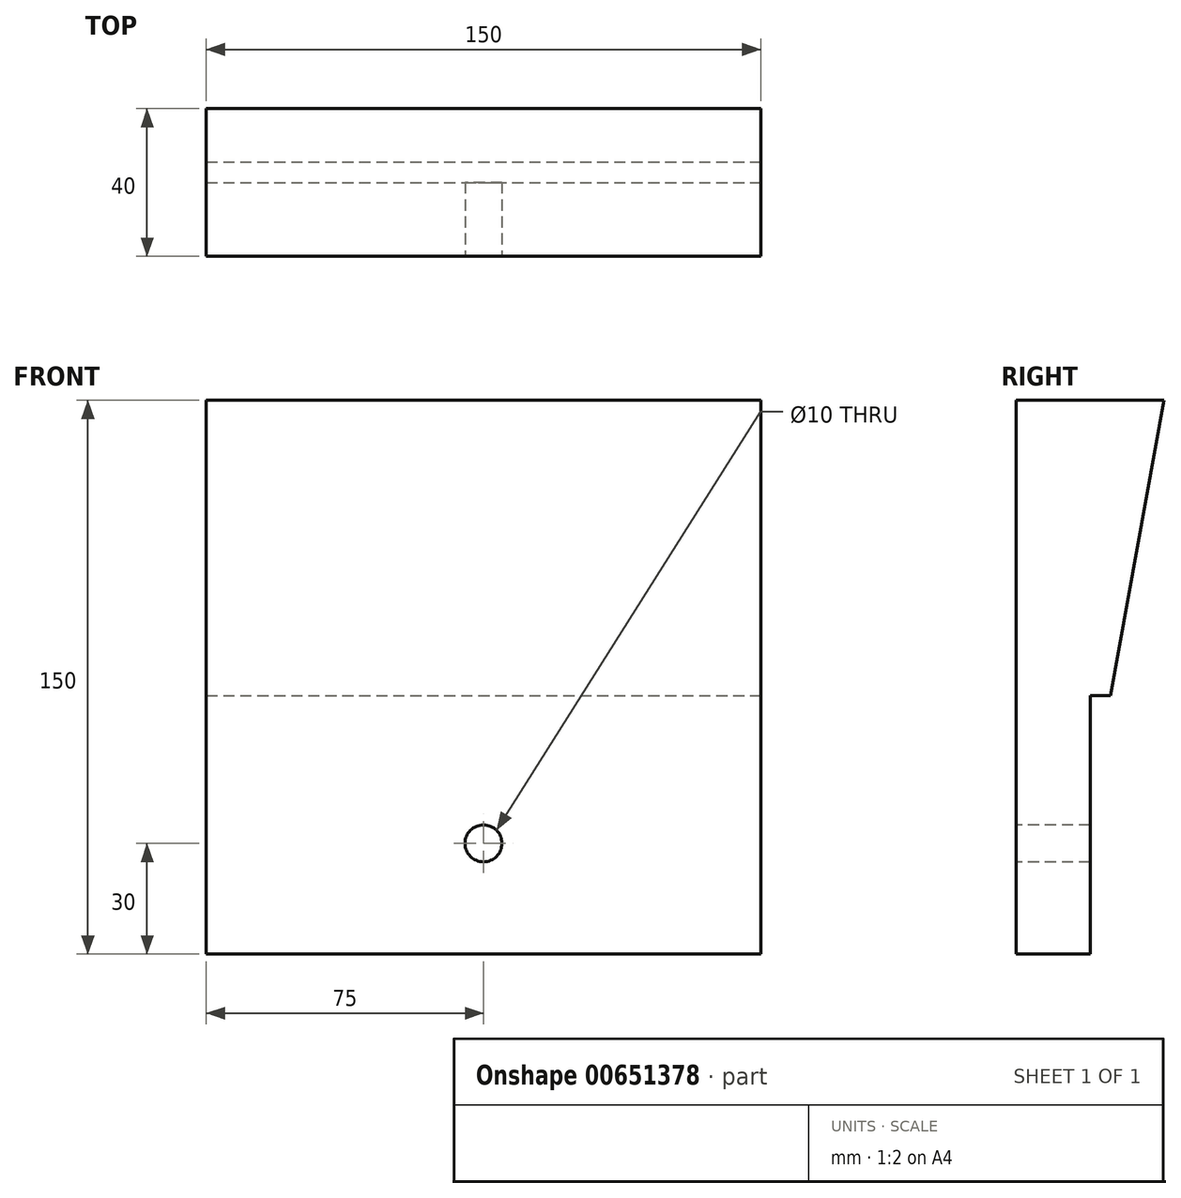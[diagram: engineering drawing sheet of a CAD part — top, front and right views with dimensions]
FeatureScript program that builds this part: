
annotation { "Feature Type Name" : "Feature", "Feature Type Description" : "" }
export const myFeature = defineFeature(function(context is Context, id is Id, definition is map)
    precondition{}
    {
        {
            var Q0;
            Q0=qCreatedBy(makeId("Front.planeOp"),FACE);
            var sketch = newSketch(context, id + "F0", { "sketchPlane" : qUnion([Q0])});
            skLineSegment(sketch, "E0.bottom", {"start": v(75, 75) * mm, "end": v(-75, 75) * mm});
            skLineSegment(sketch, "E0.top", {"start": v(75, -75) * mm, "end": v(-75, -75) * mm});
            skLineSegment(sketch, "E0.left", {"start": v(75, 75) * mm, "end": v(75, -75) * mm});
            skLineSegment(sketch, "E0.right", {"start": v(-75, 75) * mm, "end": v(-75, -75) * mm});
            skPoint(sketch, "E0.middle", {"position": v(0, 0) * mm});
            skSolve(sketch);
        }
        {
            var Q0;
            Q0 = qSketchRegion(id + "F0", true);
            extrude(context, id + "F1", {"entities" : qUnion([Q0]), "depth" : 20 * mm, "offsetDistance" : 25 * mm});
        }
        {
            var Q0;
            Q0=makeQuery(id+"F1.opExtrude","CAP_FACE",FACE,{"disambiguationData":[OSD([sQuery(id+"F0.wireOp",EDGE,"E0.bottom"),sQuery(id+"F0.wireOp",EDGE,"E0.top"),sQuery(id+"F0.wireOp",EDGE,"E0.left"),sQuery(id+"F0.wireOp",EDGE,"E0.right")])],"isStart":true});
            var sketch = newSketch(context, id + "F2", { "sketchPlane" : qUnion([Q0])});
            skLineSegment(sketch, "E1.bottom", {"start": v(75, 75) * mm, "end": v(-75, 75) * mm});
            skLineSegment(sketch, "E1.top", {"start": v(75, -5) * mm, "end": v(-75, -5) * mm});
            skLineSegment(sketch, "E1.left", {"start": v(75, 75) * mm, "end": v(75, -5) * mm});
            skLineSegment(sketch, "E1.right", {"start": v(-75, 75) * mm, "end": v(-75, -5) * mm});
            skSolve(sketch);
        }
        {
            var Q0;
            Q0=makeQuery(id+"F2.imprint","IMPRINT",FACE,{"disambiguationData":[TD([[makeQuery(id+"F2.imprint","IMPRINT",EDGE,{"derivedFrom":sQuery(id+"F2.wireOp",EDGE,"E1.bottom")}),-1.0]])]});
            var Q1;
            Q1=sQuery(id+"F2.wireOp",EDGE,"E1.top");
            var Q2;
            Q2=sQuery(id+"F2.wireOp",EDGE,"E1.bottom");
            var Q3;
            Q3=sQuery(id+"F2.wireOp",EDGE,"E1.left");
            var Q4;
            Q4=sQuery(id+"F2.wireOp",EDGE,"E1.right");
            extrude(context, id + "F3", {"entities" : qUnion([Q0]), "operationType" : NewBodyOperationType.ADD, "surfaceEntities" : qUnion([Q1, Q2, Q3, Q4]), "depth" : 20 * mm, "offsetDistance" : 25 * mm});
        }
        {
            var Q0;
            Q0=makeQuery(id+"F3.boolean.opBoolean","MERGE",FACE,{"derivedFrom":[makeQuery(id+"F1.opExtrude","SWEPT_FACE",FACE,{"disambiguationData":[OSD([sQuery(id+"F0.wireOp",EDGE,"E0.left")])]}),makeQuery(id+"F3.opExtrude","SWEPT_FACE",FACE,{"disambiguationData":[OSD([sQuery(id+"F2.wireOp",EDGE,"E1.right")])]})]});
            var sketch = newSketch(context, id + "F4", { "sketchPlane" : qUnion([Q0])});
            skLineSegment(sketch, "E2", {"start": v(20, 75) * mm, "end": v(5.59, -5) * mm});
            skLineSegment(sketch, "E3", {"start": v(5.59, -5) * mm, "end": v(20, -5) * mm});
            skLineSegment(sketch, "E4", {"start": v(20, -5) * mm, "end": v(20, 75) * mm});
            skSolve(sketch);
        }
        {
            var Q0;
            Q0 = qSketchRegion(id + "F4", true);
            extrude(context, id + "F5", {"entities" : qUnion([Q0]), "operationType" : NewBodyOperationType.REMOVE, "endBound" : BoundingType.THROUGH_ALL, "oppositeDirection" : true, "depth" : 25 * mm, "offsetDistance" : 25 * mm});
        }
        {
            var Q0;
            Q0=makeQuery(id+"F1.opExtrude","CAP_FACE",FACE,{"disambiguationData":[OSD([sQuery(id+"F0.wireOp",EDGE,"E0.bottom"),sQuery(id+"F0.wireOp",EDGE,"E0.top"),sQuery(id+"F0.wireOp",EDGE,"E0.left"),sQuery(id+"F0.wireOp",EDGE,"E0.right")])],"isStart":false});
            var sketch = newSketch(context, id + "F6", { "sketchPlane" : qUnion([Q0])});
            skCircle(sketch, "E5", {"center": v(0, -45) * mm, "radius": 5 * mm});
            skSolve(sketch);
        }
        {
            var Q0;
            Q0=makeQuery(id+"F6.imprint","IMPRINT",FACE,{"disambiguationData":[TD([[makeQuery(id+"F6.imprint","IMPRINT",EDGE,{"derivedFrom":sQuery(id+"F6.wireOp",EDGE,"4ceff230-ef04-4402-a865-7177a91ece7b")}),1.0]])]});
            var Q1;
            Q1 = qSketchRegion(id + "F6", true);
            extrude(context, id + "F7", {"entities" : qUnion([Q0, Q1]), "operationType" : NewBodyOperationType.REMOVE, "endBound" : BoundingType.THROUGH_ALL, "oppositeDirection" : true, "depth" : 25 * mm, "offsetDistance" : 25 * mm});
        }
    });
